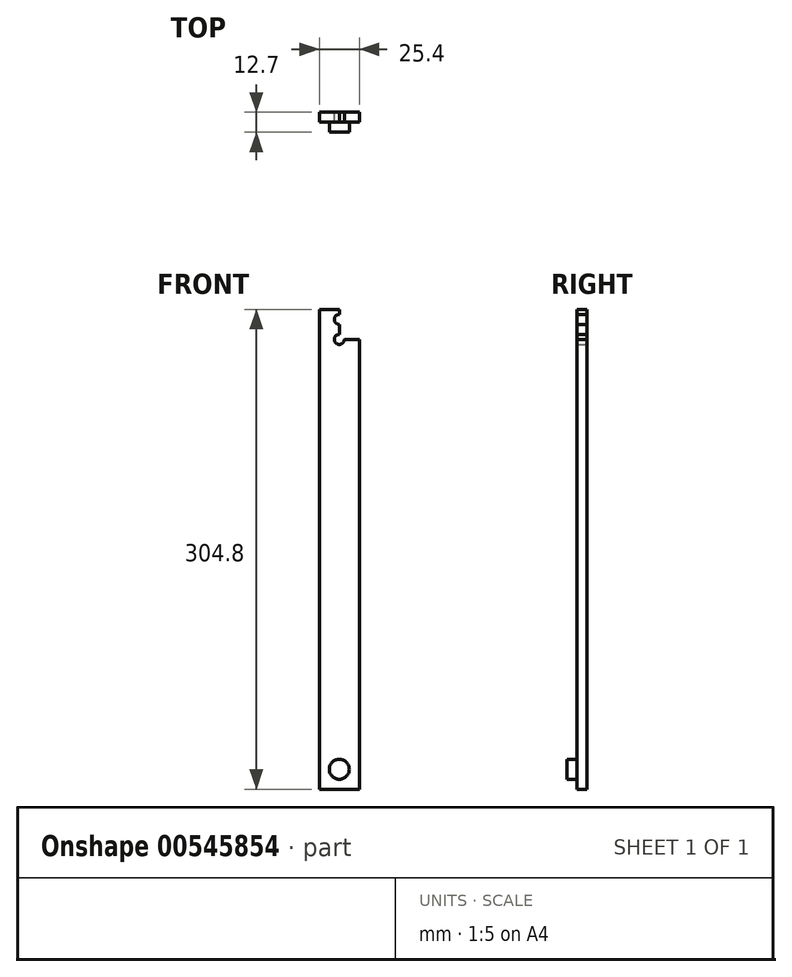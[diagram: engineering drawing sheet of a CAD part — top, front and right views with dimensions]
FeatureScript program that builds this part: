
annotation { "Feature Type Name" : "Feature", "Feature Type Description" : "" }
export const myFeature = defineFeature(function(context is Context, id is Id, definition is map)
    precondition{}
    {
        {
            var Q0;
            Q0=qCreatedBy(makeId("Front.planeOp"),FACE);
            var sketch = newSketch(context, id + "F0", { "sketchPlane" : qUnion([Q0])});
            skLineSegment(sketch, "E0.bottom", {"start": v(-10.6, 266.7) * mm, "end": v(14.8, 266.7) * mm});
            skLineSegment(sketch, "E0.top", {"start": v(-10.6, -38.1) * mm, "end": v(14.8, -38.1) * mm});
            skLineSegment(sketch, "E0.left", {"start": v(-10.6, 266.7) * mm, "end": v(-10.6, -38.1) * mm});
            skLineSegment(sketch, "E0.right", {"start": v(14.8, 266.7) * mm, "end": v(14.8, -38.1) * mm});
            skLineSegment(sketch, "E1", {"start": v(-10.6, 260.35) * mm, "end": v(14.8, 260.35) * mm});
            skLineSegment(sketch, "E2", {"start": v(-10.6, 247.65) * mm, "end": v(14.8, 247.65) * mm});
            skLineSegment(sketch, "E3", {"start": v(2.1, 266.7) * mm, "end": v(2.1, 247.65) * mm});
            skCircle(sketch, "E4", {"center": v(2.1, 260.35) * mm, "radius": 3.18 * mm});
            skCircle(sketch, "E5", {"center": v(2.1, 247.65) * mm, "radius": 3.18 * mm});
            skLineSegment(sketch, "E6", {"start": v(2.1, -38.1) * mm, "end": v(2.1, -25.4) * mm});
            skCircle(sketch, "E7", {"center": v(2.1, -25.4) * mm, "radius": 6.35 * mm});
            skSolve(sketch);
        }
        {
            var Q0;
            Q0=makeQuery(id+"F0.imprint","IMPRINT",FACE,{"disambiguationData":[TD([[makeQuery(id+"F0.imprint","IMPRINT",EDGE,{"derivedFrom":sQuery(id+"F0.wireOp",EDGE,"E7")}),1.0]])]});
            var Q1;
            {var subQ1=sQuery(id+"F0.wireOp",EDGE,"E0.bottom");var subQ5=sQuery(id+"F0.wireOp",EDGE,"E0.left");var subQ6=makeQuery(id+"F0.imprint","INTERSECT",VERTEX,{"derivedFrom":[subQ1,subQ5]});Q1=makeQuery(id+"F0.imprint","IMPRINT",FACE,{"disambiguationData":[TD([[makeQuery(id+"F0.imprint","IMPRINT",EDGE,{"disambiguationData":[TD([[subQ6,-1.0]])],"derivedFrom":subQ1}),-1.0]])]});}
            var Q2;
            {var subQ5=sQuery(id+"F0.wireOp",EDGE,"E1");var subQ6=sQuery(id+"F0.wireOp",EDGE,"E0.left");var subQ7=makeQuery(id+"F0.imprint","INTERSECT",VERTEX,{"derivedFrom":[subQ6,subQ5]});Q2=makeQuery(id+"F0.imprint","IMPRINT",FACE,{"disambiguationData":[TD([[makeQuery(id+"F0.imprint","IMPRINT",EDGE,{"disambiguationData":[TD([[subQ7,-1.0]])],"derivedFrom":subQ6}),1.0]])]});}
            var Q3;
            {var subQ0=sQuery(id+"F0.wireOp",EDGE,"E3");var subQ1=sQuery(id+"F0.wireOp",EDGE,"E1");var subQ2=makeQuery(id+"F0.imprint","INTERSECT",VERTEX,{"derivedFrom":[subQ1,subQ0]});Q3=makeQuery(id+"F0.imprint","IMPRINT",FACE,{"disambiguationData":[TD([[makeQuery(id+"F0.imprint","IMPRINT",EDGE,{"disambiguationData":[TD([[subQ2,-1.0]])],"derivedFrom":subQ1}),-1.0]])]});}
            var Q4;
            {var subQ0=sQuery(id+"F0.wireOp",EDGE,"E3");var subQ1=sQuery(id+"F0.wireOp",EDGE,"E2");var subQ2=makeQuery(id+"F0.imprint","INTERSECT",VERTEX,{"derivedFrom":[subQ1,subQ0]});Q4=makeQuery(id+"F0.imprint","IMPRINT",FACE,{"disambiguationData":[TD([[makeQuery(id+"F0.imprint","IMPRINT",EDGE,{"disambiguationData":[TD([[subQ2,1.0]])],"derivedFrom":subQ1}),1.0]])]});}
            var Q5;
            {var subQ0=sQuery(id+"F0.wireOp",EDGE,"E4");var subQ1=sQuery(id+"F0.wireOp",EDGE,"E1");var subQ2=makeQuery(id+"F0.imprint","INTERSECT",VERTEX,{"disambiguationData":[OD(0.0)],"derivedFrom":[subQ1,subQ0]});Q5=makeQuery(id+"F0.imprint","IMPRINT",FACE,{"disambiguationData":[TD([[makeQuery(id+"F0.imprint","IMPRINT",EDGE,{"disambiguationData":[TD([[subQ2,-1.0]])],"derivedFrom":subQ1}),1.0]])]});}
            var Q6;
            {var subQ0=sQuery(id+"F0.wireOp",EDGE,"E2");var subQ1=makeQuery(id+"F0.imprint","INTERSECT",VERTEX,{"derivedFrom":[subQ0,sQuery(id+"F0.wireOp",EDGE,"E3")]});Q6=makeQuery(id+"F0.imprint","IMPRINT",FACE,{"disambiguationData":[TD([[makeQuery(id+"F0.imprint","IMPRINT",EDGE,{"disambiguationData":[TD([[subQ1,1.0]])],"derivedFrom":subQ0}),-1.0]])]});}
            var Q7;
            {var subQ0=sQuery(id+"F0.wireOp",EDGE,"E4");var subQ1=sQuery(id+"F0.wireOp",EDGE,"E1");var subQ2=makeQuery(id+"F0.imprint","INTERSECT",VERTEX,{"disambiguationData":[OD(0.0)],"derivedFrom":[subQ1,subQ0]});Q7=makeQuery(id+"F0.imprint","IMPRINT",FACE,{"disambiguationData":[TD([[makeQuery(id+"F0.imprint","IMPRINT",EDGE,{"disambiguationData":[TD([[subQ2,-1.0]])],"derivedFrom":subQ1}),-1.0]])]});}
            var Q8;
            {var subQ0=sQuery(id+"F0.wireOp",EDGE,"E3");var subQ1=sQuery(id+"F0.wireOp",EDGE,"E1");var subQ2=makeQuery(id+"F0.imprint","INTERSECT",VERTEX,{"derivedFrom":[subQ1,subQ0]});Q8=makeQuery(id+"F0.imprint","IMPRINT",FACE,{"disambiguationData":[TD([[makeQuery(id+"F0.imprint","IMPRINT",EDGE,{"disambiguationData":[TD([[subQ2,-1.0]])],"derivedFrom":subQ1}),1.0]])]});}
            var Q9;
            {var subQ0=sQuery(id+"F0.wireOp",EDGE,"E3");var subQ1=sQuery(id+"F0.wireOp",EDGE,"E2");var subQ2=makeQuery(id+"F0.imprint","INTERSECT",VERTEX,{"derivedFrom":[subQ1,subQ0]});Q9=makeQuery(id+"F0.imprint","IMPRINT",FACE,{"disambiguationData":[TD([[makeQuery(id+"F0.imprint","IMPRINT",EDGE,{"disambiguationData":[TD([[subQ2,-1.0]])],"derivedFrom":subQ1}),1.0]])]});}
            var Q10;
            {var subQ1=sQuery(id+"F0.wireOp",EDGE,"E0.bottom");var subQ5=sQuery(id+"F0.wireOp",EDGE,"E0.right");var subQ6=makeQuery(id+"F0.imprint","INTERSECT",VERTEX,{"derivedFrom":[subQ1,subQ5]});Q10=makeQuery(id+"F0.imprint","IMPRINT",FACE,{"disambiguationData":[TD([[makeQuery(id+"F0.imprint","IMPRINT",EDGE,{"disambiguationData":[TD([[subQ6,1.0]])],"derivedFrom":subQ1}),-1.0]])]});}
            var Q11;
            {var subQ6=sQuery(id+"F0.wireOp",EDGE,"E0.right");var subQ9=sQuery(id+"F0.wireOp",EDGE,"E1");var subQ10=makeQuery(id+"F0.imprint","INTERSECT",VERTEX,{"derivedFrom":[subQ6,subQ9]});Q11=makeQuery(id+"F0.imprint","IMPRINT",FACE,{"disambiguationData":[TD([[makeQuery(id+"F0.imprint","IMPRINT",EDGE,{"disambiguationData":[TD([[subQ10,-1.0]])],"derivedFrom":subQ6}),-1.0]])]});}
            var Q12;
            Q12=makeQuery(id+"F0.imprint","IMPRINT",FACE,{"disambiguationData":[TD([[makeQuery(id+"F0.imprint","IMPRINT",EDGE,{"derivedFrom":sQuery(id+"F0.wireOp",EDGE,"E7")}),-1.0]])]});
            var Q13;
            Q13=sQuery(id+"F0.wireOp",EDGE,"E0.bottom");
            var Q14;
            Q14=sQuery(id+"F0.wireOp",EDGE,"E4");
            var Q15;
            Q15=sQuery(id+"F0.wireOp",EDGE,"E0.right");
            var Q16;
            Q16=sQuery(id+"F0.wireOp",EDGE,"E3");
            var Q17;
            Q17=sQuery(id+"F0.wireOp",EDGE,"E0.left");
            var Q18;
            Q18=sQuery(id+"F0.wireOp",EDGE,"E2");
            var Q19;
            Q19=sQuery(id+"F0.wireOp",EDGE,"E0.top");
            var Q20;
            Q20=sQuery(id+"F0.wireOp",EDGE,"E6");
            var Q21;
            Q21=sQuery(id+"F0.wireOp",EDGE,"E5");
            var Q22;
            Q22=sQuery(id+"F0.wireOp",EDGE,"E7");
            var Q23;
            Q23=sQuery(id+"F0.wireOp",EDGE,"E1");
            extrude(context, id + "F1", {"entities" : qUnion([Q0, Q1, Q2, Q3, Q4, Q5, Q6, Q7, Q8, Q9, Q10, Q11, Q12]), "surfaceEntities" : qUnion([Q13, Q14, Q15, Q16, Q17, Q18, Q19, Q20, Q21, Q22, Q23]), "depth" : 6.35 * mm, "offsetDistance" : 25.4 * mm});
        }
        {
            var Q0;
            Q0=makeQuery(id+"F0.imprint","IMPRINT",FACE,{"disambiguationData":[TD([[makeQuery(id+"F0.imprint","IMPRINT",EDGE,{"derivedFrom":sQuery(id+"F0.wireOp",EDGE,"E7")}),1.0]])]});
            var Q1;
            Q1=sQuery(id+"F0.wireOp",EDGE,"E7");
            extrude(context, id + "F2", {"entities" : qUnion([Q0]), "operationType" : NewBodyOperationType.ADD, "surfaceEntities" : qUnion([Q1]), "depth" : 12.7 * mm, "offsetDistance" : 25.4 * mm});
        }
        {
            var Q0;
            {var subQ0=sQuery(id+"F0.wireOp",EDGE,"E3");var subQ1=sQuery(id+"F0.wireOp",EDGE,"E2");var subQ2=makeQuery(id+"F0.imprint","INTERSECT",VERTEX,{"derivedFrom":[subQ1,subQ0]});Q0=makeQuery(id+"F0.imprint","IMPRINT",FACE,{"disambiguationData":[TD([[makeQuery(id+"F0.imprint","IMPRINT",EDGE,{"disambiguationData":[TD([[subQ2,-1.0]])],"derivedFrom":subQ1}),1.0]])]});}
            var Q1;
            {var subQ0=sQuery(id+"F0.wireOp",EDGE,"E3");var subQ1=sQuery(id+"F0.wireOp",EDGE,"E2");var subQ2=makeQuery(id+"F0.imprint","INTERSECT",VERTEX,{"derivedFrom":[subQ1,subQ0]});Q1=makeQuery(id+"F0.imprint","IMPRINT",FACE,{"disambiguationData":[TD([[makeQuery(id+"F0.imprint","IMPRINT",EDGE,{"disambiguationData":[TD([[subQ2,1.0]])],"derivedFrom":subQ1}),1.0]])]});}
            var Q2;
            {var subQ0=sQuery(id+"F0.wireOp",EDGE,"E2");var subQ1=makeQuery(id+"F0.imprint","INTERSECT",VERTEX,{"derivedFrom":[subQ0,sQuery(id+"F0.wireOp",EDGE,"E3")]});Q2=makeQuery(id+"F0.imprint","IMPRINT",FACE,{"disambiguationData":[TD([[makeQuery(id+"F0.imprint","IMPRINT",EDGE,{"disambiguationData":[TD([[subQ1,1.0]])],"derivedFrom":subQ0}),-1.0]])]});}
            var Q3;
            {var subQ0=sQuery(id+"F0.wireOp",EDGE,"E3");var subQ1=sQuery(id+"F0.wireOp",EDGE,"E1");var subQ2=makeQuery(id+"F0.imprint","INTERSECT",VERTEX,{"derivedFrom":[subQ1,subQ0]});Q3=makeQuery(id+"F0.imprint","IMPRINT",FACE,{"disambiguationData":[TD([[makeQuery(id+"F0.imprint","IMPRINT",EDGE,{"disambiguationData":[TD([[subQ2,-1.0]])],"derivedFrom":subQ1}),1.0]])]});}
            var Q4;
            {var subQ0=sQuery(id+"F0.wireOp",EDGE,"E4");var subQ1=sQuery(id+"F0.wireOp",EDGE,"E1");var subQ2=makeQuery(id+"F0.imprint","INTERSECT",VERTEX,{"disambiguationData":[OD(0.0)],"derivedFrom":[subQ1,subQ0]});Q4=makeQuery(id+"F0.imprint","IMPRINT",FACE,{"disambiguationData":[TD([[makeQuery(id+"F0.imprint","IMPRINT",EDGE,{"disambiguationData":[TD([[subQ2,-1.0]])],"derivedFrom":subQ1}),1.0]])]});}
            var Q5;
            {var subQ0=sQuery(id+"F0.wireOp",EDGE,"E4");var subQ1=sQuery(id+"F0.wireOp",EDGE,"E1");var subQ2=makeQuery(id+"F0.imprint","INTERSECT",VERTEX,{"disambiguationData":[OD(0.0)],"derivedFrom":[subQ1,subQ0]});Q5=makeQuery(id+"F0.imprint","IMPRINT",FACE,{"disambiguationData":[TD([[makeQuery(id+"F0.imprint","IMPRINT",EDGE,{"disambiguationData":[TD([[subQ2,-1.0]])],"derivedFrom":subQ1}),-1.0]])]});}
            var Q6;
            {var subQ0=sQuery(id+"F0.wireOp",EDGE,"E3");var subQ1=sQuery(id+"F0.wireOp",EDGE,"E1");var subQ2=makeQuery(id+"F0.imprint","INTERSECT",VERTEX,{"derivedFrom":[subQ1,subQ0]});Q6=makeQuery(id+"F0.imprint","IMPRINT",FACE,{"disambiguationData":[TD([[makeQuery(id+"F0.imprint","IMPRINT",EDGE,{"disambiguationData":[TD([[subQ2,-1.0]])],"derivedFrom":subQ1}),-1.0]])]});}
            var Q7;
            Q7=sQuery(id+"F0.wireOp",EDGE,"E5");
            var Q8;
            Q8=sQuery(id+"F0.wireOp",EDGE,"E4");
            extrude(context, id + "F3", {"entities" : qUnion([Q0, Q1, Q2, Q3, Q4, Q5, Q6]), "operationType" : NewBodyOperationType.REMOVE, "surfaceEntities" : qUnion([Q7, Q8]), "depth" : 24.64 * mm, "offsetDistance" : 25.4 * mm});
        }
    });
